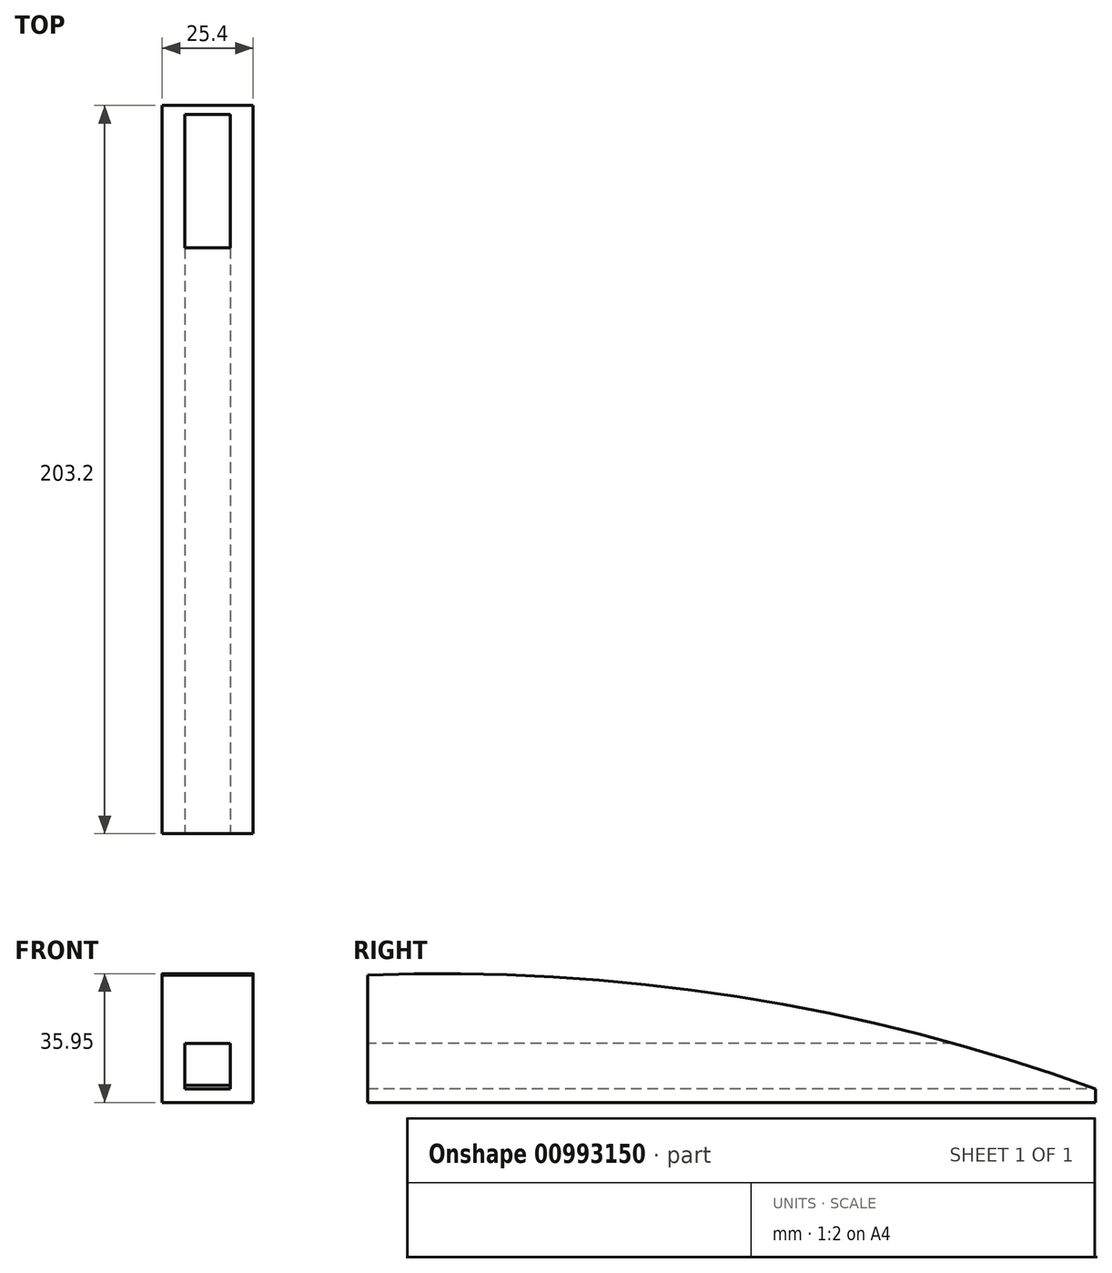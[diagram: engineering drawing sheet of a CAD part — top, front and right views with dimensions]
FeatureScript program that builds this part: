
annotation { "Feature Type Name" : "Feature", "Feature Type Description" : "" }
export const myFeature = defineFeature(function(context is Context, id is Id, definition is map)
    precondition{}
    {
        {
            var Q0;
            Q0=qCreatedBy(makeId("Right.planeOp"),FACE);
            var sketch = newSketch(context, id + "F0", { "sketchPlane" : qUnion([Q0])});
            skLineSegment(sketch, "E0.bottom", {"start": v(-77.32, 22.07) * mm, "end": v(125.88, 22.07) * mm});
            skLineSegment(sketch, "E0.top", {"start": v(-77.32, 18.26) * mm, "end": v(125.88, 18.26) * mm});
            skLineSegment(sketch, "E0.left", {"start": v(-77.32, 22.07) * mm, "end": v(-77.32, 18.26) * mm});
            skLineSegment(sketch, "E0.right", {"start": v(125.88, 22.07) * mm, "end": v(125.88, 18.26) * mm});
            skLineSegment(sketch, "E1", {"start": v(-77.32, 22.07) * mm, "end": v(-77.32, 53.82) * mm});
            skArc(sketch, "E2", {"start": v(125.88, 22.07) * mm, "mid": v(25.82, 47.79) * mm, "end": v(-77.32, 53.82) * mm});
            skSolve(sketch);
        }
        {
            var Q0;
            Q0=makeQuery(id+"F0.imprint","IMPRINT",FACE,{"disambiguationData":[TD([[makeQuery(id+"F0.imprint","IMPRINT",EDGE,{"derivedFrom":sQuery(id+"F0.wireOp",EDGE,"E0.bottom")}),1.0]])]});
            var Q1;
            Q1=makeQuery(id+"F0.imprint","IMPRINT",FACE,{"disambiguationData":[TD([[makeQuery(id+"F0.imprint","IMPRINT",EDGE,{"derivedFrom":sQuery(id+"F0.wireOp",EDGE,"E0.bottom")}),-1.0]])]});
            extrude(context, id + "F1", {"entities" : qUnion([Q0, Q1]), "depth" : 25.4 * mm, "offsetDistance" : 25.4 * mm});
        }
        {
            var Q0;
            Q0=makeQuery(id+"F1.opExtrude","SWEPT_FACE",FACE,{"disambiguationData":[OSD([sQuery(id+"F0.wireOp",EDGE,"E0.left"),sQuery(id+"F0.wireOp",EDGE,"E1")])]});
            var sketch = newSketch(context, id + "F2", { "sketchPlane" : qUnion([Q0])});
            skLineSegment(sketch, "E3.bottom", {"start": v(19.05, 22.07) * mm, "end": v(6.35, 22.07) * mm});
            skLineSegment(sketch, "E3.top", {"start": v(19.05, 34.77) * mm, "end": v(6.35, 34.77) * mm});
            skLineSegment(sketch, "E3.left", {"start": v(19.05, 22.07) * mm, "end": v(19.05, 34.77) * mm});
            skLineSegment(sketch, "E3.right", {"start": v(6.35, 22.07) * mm, "end": v(6.35, 34.77) * mm});
            skPoint(sketch, "E3.middle", {"position": v(12.7, 28.42) * mm});
            skPoint(sketch, "E3.middle.positionSnap0", {"position": v(12.7, 18.26) * mm});
            skPoint(sketch, "E3.centerSnap0", {"position": v(12.7, 18.26) * mm});
            skSolve(sketch);
        }
        {
            var Q0;
            Q0=makeQuery(id+"F2.imprint","IMPRINT",FACE,{"disambiguationData":[TD([[makeQuery(id+"F2.imprint","IMPRINT",EDGE,{"derivedFrom":sQuery(id+"F2.wireOp",EDGE,"E3.bottom")}),-1.0]])]});
            extrude(context, id + "F3", {"entities" : qUnion([Q0]), "operationType" : NewBodyOperationType.REMOVE, "oppositeDirection" : true, "depth" : 200.66 * mm, "offsetDistance" : 25.4 * mm});
        }
    });
